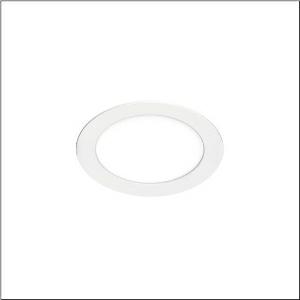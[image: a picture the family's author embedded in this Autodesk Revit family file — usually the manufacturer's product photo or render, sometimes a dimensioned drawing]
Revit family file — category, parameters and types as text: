
# Revit family: lunis_41_flat_51dr10mfhcb
name_source: partatom
category: Lighting Fixtures
units: mm (PartAtom-declared; Revit-internal decimal feet)

## family parameters
Cut with Voids When Loaded = No
Host = Face
Light Source = No
Part Type = Normal
Room Calculation Point = No
Round Connector Dimension = Use Diameter
Shared = No

## types (1)
- --- (1 x LED, 2500 lm, 19.5 W, 6500K)
    Apparent Load = 20 VA
    CIE Flux Codes = 49 80 96 100 100
    Color Rendering = 80
    Color Temperature = 6500K
    Default Elevation = 1800 mm
    Description = Lunis 41,  Flat, downlight, light emission: direct distribution, LED rated luminous flux: 2.430lm, light colour: 840/865, mains connection: 230V, AC, 50/60Hz, housing, round, of aluminium, coated, traffic white (RAL 9016), diameter: 225mm, protection rating (complete): IP20, protection rating (on room side): IP44, insulation class (complete): insulation class II (safety insulation), certification: CE, permissible ambient temperature for indoor applications: -20..+40°C, packaging unit: 1 piece
    Height = 0 mm  [stored 0 ft]
    Lamp = 1 x LED
    Lamp Light Flux = 2500 lm
    Lamp Power = 19.5 W
    Lamp count = 1
    Length = 225 mm
    Luminous efficacy = 128 lm/W
    Manufacturer = Siteco
    ModVariant = No
    Model = 51DR10MFHCB
    Mounting Place = Ceiling
    Mounting Type = Recessed
    Number of Poles = 1
    OnlyDefault = Yes
    Power Factor = 1
    Product Name = Lunis 41 Flat
    Product group = downlight
    ProductGroupID = 401
    Protection Class = Protection class II
    Protection Degree = IP 20
    RLX_Detail_Level = 1
    RLX_Emergency_Light_Flux = 0 lm
    RLX_Emergency_Type = 0
    RLX_Emergency_Type_DB = No
    RlxData = <blob elided: 11581 chars, md5=fd5b6ace>
    Socket = socket
    Standby Power = 0 W
    System Light Flux = 2500 lm
    System Power = 20 W
    Type Comments = individual setting: colour temperature 6500K
    Type Image = l_1340923.jpg
    URL = http://relux.com
    VarID = @adj_018935
    Voltage = 0 V
    Weight = 0.00 kg
    Width = 0 mm  [stored 0 ft]

note: [stored X ft] marks values corroborated as IEEE doubles in the binary element streams (Revit-internal decimal feet)

## geometry (parser evidence)
native form markers: Sweep x10
no freeform markers — native parametric forms only
